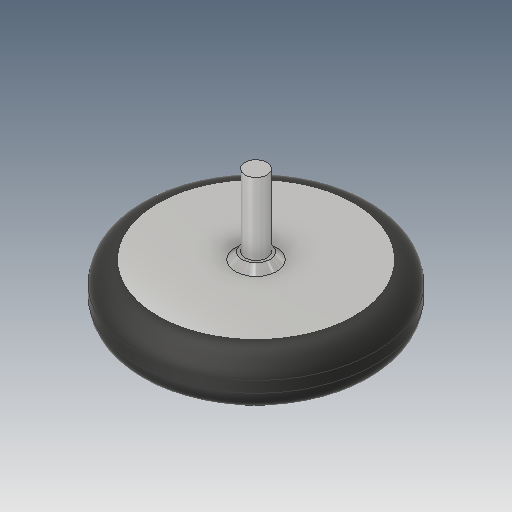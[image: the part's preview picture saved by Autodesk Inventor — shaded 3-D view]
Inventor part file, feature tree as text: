
AUTODESK INVENTOR PART (.ipt)
format: ipt  version: 2018 (Build 220112000, 112)  size: 164,352 bytes
history: native  units: in
note: dims shown in document units (in); Inventor stores cm internally (conversion verified against a paired STEP export)
features: other x3, sketch x3
ambient origin geometry x8: Origin, YZ Plane, XZ Plane, XY Plane, X Axis, Y Axis, Z Axis, Center Point
bodies: Solid1 (feature_tree)
feature tree (6):
  other  "10-001-ACTR.ipt"
  other  "Solid1::10-001-ACTR.ipt"
  other  "TaggingFeature1"
  sketch  "Sketch1"  dims[d0=0.3937in]
  sketch  "Sketch2"
  sketch  "Sketch3"
